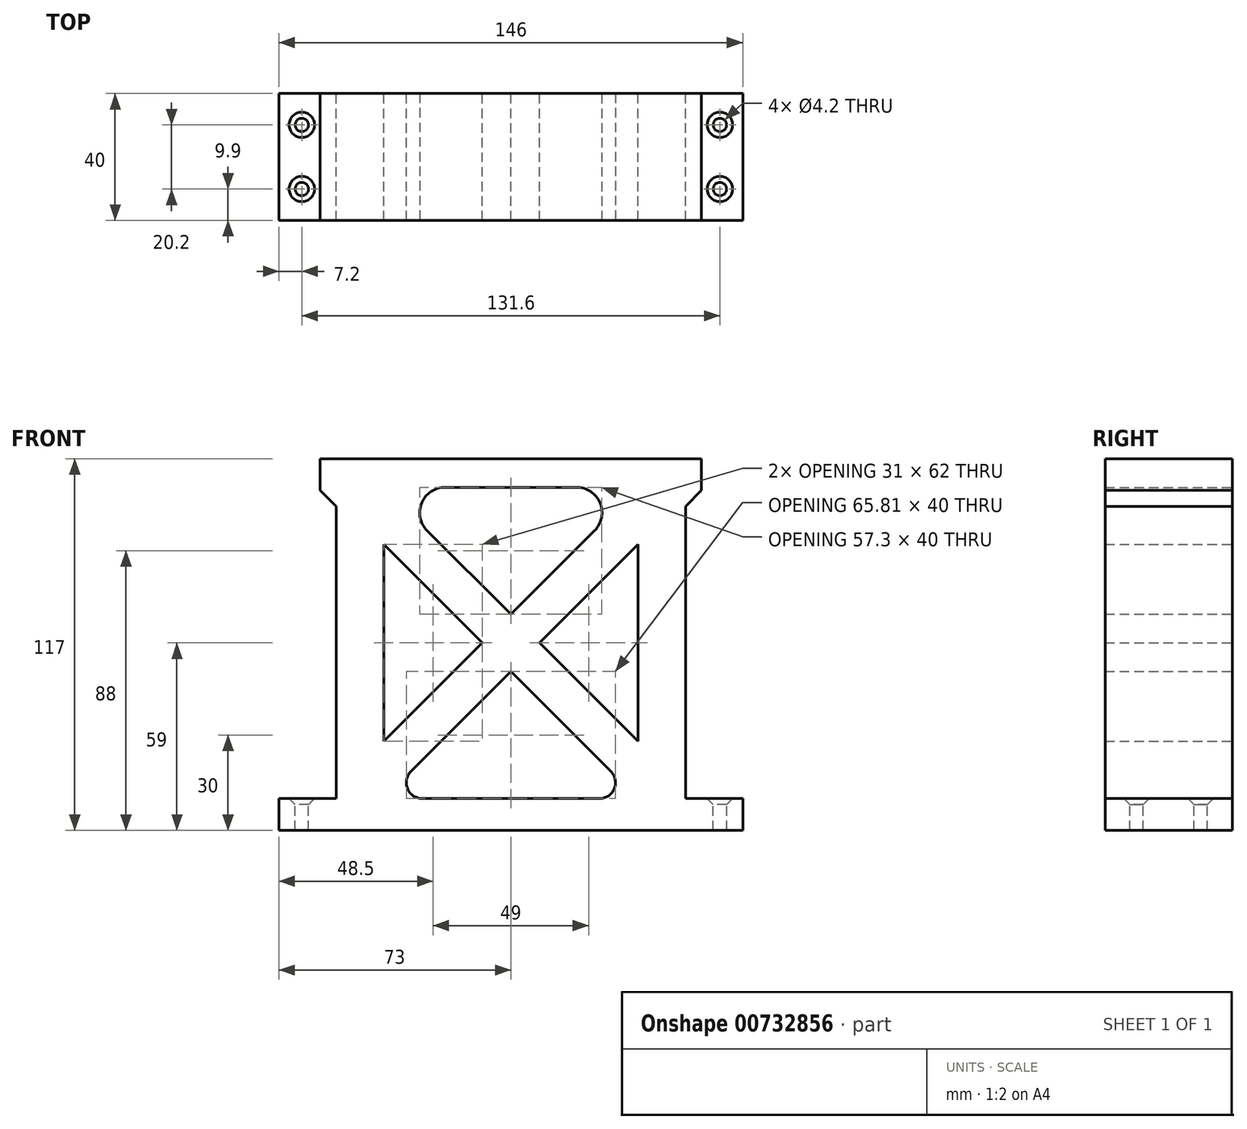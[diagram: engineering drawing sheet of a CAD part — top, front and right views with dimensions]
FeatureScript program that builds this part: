
annotation { "Feature Type Name" : "Feature", "Feature Type Description" : "" }
export const myFeature = defineFeature(function(context is Context, id is Id, definition is map)
    precondition{}
    {
        {
            var Q0;
            Q0=qCreatedBy(makeId("Front.planeOp"),FACE);
            var sketch = newSketch(context, id + "F0", { "sketchPlane" : qUnion([Q0])});
            skLineSegment(sketch, "E0", {"start": v(-73, 0) * mm, "end": v(-73, 10) * mm});
            skLineSegment(sketch, "E1", {"start": v(-73, 10) * mm, "end": v(-55, 10) * mm});
            skLineSegment(sketch, "E2", {"start": v(-55, 10) * mm, "end": v(-55, 107) * mm});
            skLineSegment(sketch, "E3", {"start": v(-55, 107) * mm, "end": v(-60, 107) * mm});
            skLineSegment(sketch, "E4", {"start": v(-60, 107) * mm, "end": v(-60, 117) * mm});
            skLineSegment(sketch, "E5", {"start": v(-60, 117) * mm, "end": v(0, 117) * mm});
            skLineSegment(sketch, "E6", {"start": v(0, 0) * mm, "end": v(-73, 0) * mm});
            skLineSegment(sketch, "E7", {"start": v(-40, 121.48) * mm, "end": v(-40, -14.49) * mm, "construction": true});
            skLineSegment(sketch, "E8", {"start": v(-55, 10) * mm, "end": v(13, 10) * mm, "construction": true});
            skLineSegment(sketch, "E9", {"start": v(-40, 28) * mm, "end": v(15.98, 83.98) * mm, "construction": true});
            skLineSegment(sketch, "E10", {"start": v(-40, 10) * mm, "end": v(0, 50) * mm, "construction": true});
            skLineSegment(sketch, "E11", {"start": v(0, 50) * mm, "end": v(-40, 90) * mm, "construction": true});
            skLineSegment(sketch, "E12", {"start": v(0, 68) * mm, "end": v(-51.64, 119.64) * mm, "construction": true});
            skLineSegment(sketch, "E13", {"start": v(-40, 10) * mm, "end": v(0, 50) * mm});
            skLineSegment(sketch, "E14", {"start": v(-40, 28) * mm, "end": v(-9, 59) * mm});
            skLineSegment(sketch, "E15", {"start": v(-9, 59) * mm, "end": v(-40, 90) * mm});
            skLineSegment(sketch, "E16", {"start": v(-40, 28) * mm, "end": v(-40, 90) * mm});
            skLineSegment(sketch, "E17", {"start": v(0, 68) * mm, "end": v(-40, 108) * mm});
            skLineSegment(sketch, "E18", {"start": v(-40, 108) * mm, "end": v(0, 108) * mm});
            skLineSegment(sketch, "E19", {"start": v(-40, 10) * mm, "end": v(0, 10) * mm});
            skLineSegment(sketch, "E20.MirrorCS", {"start": v(60, 117) * mm, "end": v(0, 117) * mm});
            skLineSegment(sketch, "E21.MirrorCS", {"start": v(60, 107) * mm, "end": v(60, 117) * mm});
            skLineSegment(sketch, "E22.MirrorCS", {"start": v(55, 107) * mm, "end": v(60, 107) * mm});
            skLineSegment(sketch, "E23.MirrorCS", {"start": v(55, 10) * mm, "end": v(55, 107) * mm});
            skLineSegment(sketch, "E24.MirrorCS", {"start": v(40, 28) * mm, "end": v(40, 90) * mm});
            skLineSegment(sketch, "E25.MirrorCS", {"start": v(9, 59) * mm, "end": v(40, 90) * mm});
            skLineSegment(sketch, "E26.MirrorCS", {"start": v(40, 28) * mm, "end": v(9, 59) * mm});
            skLineSegment(sketch, "E27.MirrorCS", {"start": v(40, 10) * mm, "end": v(0, 50) * mm});
            skLineSegment(sketch, "E28.MirrorCS", {"start": v(0, 68) * mm, "end": v(40, 108) * mm});
            skLineSegment(sketch, "E29.MirrorCS", {"start": v(40, 108) * mm, "end": v(0, 108) * mm});
            skLineSegment(sketch, "E30.MirrorCS", {"start": v(40, 10) * mm, "end": v(0, 10) * mm});
            skLineSegment(sketch, "E31.MirrorCS", {"start": v(0, 0) * mm, "end": v(73, 0) * mm});
            skLineSegment(sketch, "E32.MirrorCS", {"start": v(73, 0) * mm, "end": v(73, 10) * mm});
            skLineSegment(sketch, "E33.MirrorCS", {"start": v(73, 10) * mm, "end": v(55, 10) * mm});
            skSolve(sketch);
        }
        {
            var Q0;
            Q0 = qSketchRegion(id + "F0", true);
            extrude(context, id + "F1", {"entities" : qUnion([Q0]), "depth" : 40 * mm, "offsetDistance" : 25 * mm});
        }
        {
            var Q0;
            Q0=makeQuery(id+"F1.opExtrude","SWEPT_EDGE",EDGE,{"disambiguationData":[OSD([sQuery(id+"F0.wireOp",EDGE,"E17"),sQuery(id+"F0.wireOp",EDGE,"E18")])]});
            var Q1;
            Q1=makeQuery(id+"F1.opExtrude","SWEPT_EDGE",EDGE,{"disambiguationData":[OSD([sQuery(id+"F0.wireOp",EDGE,"E28.MirrorCS"),sQuery(id+"F0.wireOp",EDGE,"E29.MirrorCS")])]});
            fillet(context, id + "F2", {"entities" : qUnion([Q0, Q1]), "radius" : 8 * mm, "tangentPropagation" : true, "allowEdgeOverflow" : false});
        }
        {
            var Q0;
            Q0=makeQuery(id+"F1.opExtrude","SWEPT_EDGE",EDGE,{"disambiguationData":[OSD([sQuery(id+"F0.wireOp",EDGE,"E13"),sQuery(id+"F0.wireOp",EDGE,"E19")])]});
            var Q1;
            Q1=makeQuery(id+"F1.opExtrude","SWEPT_EDGE",EDGE,{"disambiguationData":[OSD([sQuery(id+"F0.wireOp",EDGE,"E27.MirrorCS"),sQuery(id+"F0.wireOp",EDGE,"E30.MirrorCS")])]});
            fillet(context, id + "F3", {"entities" : qUnion([Q0, Q1]), "radius" : 5 * mm, "tangentPropagation" : true, "allowEdgeOverflow" : false});
        }
        {
            var Q0;
            Q0=makeQuery(id+"F1.opExtrude","SWEPT_FACE",FACE,{"disambiguationData":[OSD([sQuery(id+"F0.wireOp",EDGE,"E1")])]});
            var sketch = newSketch(context, id + "F4", { "sketchPlane" : qUnion([Q0])});
            skPoint(sketch, "E34", {"position": v(-65.8, -9.9) * mm});
            skPoint(sketch, "E35", {"position": v(-65.8, -30.1) * mm});
            skPoint(sketch, "E36", {"position": v(65.8, -30.1) * mm});
            skPoint(sketch, "E37", {"position": v(65.8, -9.9) * mm});
            skLineSegment(sketch, "E38", {"start": v(-85.7, -20) * mm, "end": v(95.67, -20) * mm, "construction": true});
            skPoint(sketch, "E38.startSnap0", {"position": v(-73, -20) * mm});
            skSolve(sketch);
        }
        {
            var Q0;
            Q0=sQuery(id+"F4.wireOp",VERTEX,"E34");
            var Q1;
            Q1=sQuery(id+"F4.wireOp",VERTEX,"E35");
            var Q2;
            Q2=sQuery(id+"F4.wireOp",VERTEX,"E36");
            var Q3;
            Q3=sQuery(id+"F4.wireOp",VERTEX,"E37");
            var Q4;
            Q4=makeQuery(id+"F1.opExtrude","SWEPT_BODY",BODY,{"disambiguationData":[OSD([sQuery(id+"F0.wireOp",EDGE,"E0"),sQuery(id+"F0.wireOp",EDGE,"E1"),sQuery(id+"F0.wireOp",EDGE,"E2"),sQuery(id+"F0.wireOp",EDGE,"E3"),sQuery(id+"F0.wireOp",EDGE,"E4"),sQuery(id+"F0.wireOp",EDGE,"E5"),sQuery(id+"F0.wireOp",EDGE,"E6"),sQuery(id+"F0.wireOp",EDGE,"E13"),sQuery(id+"F0.wireOp",EDGE,"E14"),sQuery(id+"F0.wireOp",EDGE,"E15"),sQuery(id+"F0.wireOp",EDGE,"E16"),sQuery(id+"F0.wireOp",EDGE,"E17"),sQuery(id+"F0.wireOp",EDGE,"E18"),sQuery(id+"F0.wireOp",EDGE,"E19"),sQuery(id+"F0.wireOp",EDGE,"E20.MirrorCS"),sQuery(id+"F0.wireOp",EDGE,"E21.MirrorCS"),sQuery(id+"F0.wireOp",EDGE,"E22.MirrorCS"),sQuery(id+"F0.wireOp",EDGE,"E23.MirrorCS"),sQuery(id+"F0.wireOp",EDGE,"E24.MirrorCS"),sQuery(id+"F0.wireOp",EDGE,"E25.MirrorCS"),sQuery(id+"F0.wireOp",EDGE,"E26.MirrorCS"),sQuery(id+"F0.wireOp",EDGE,"E27.MirrorCS"),sQuery(id+"F0.wireOp",EDGE,"E28.MirrorCS"),sQuery(id+"F0.wireOp",EDGE,"E29.MirrorCS"),sQuery(id+"F0.wireOp",EDGE,"E30.MirrorCS"),sQuery(id+"F0.wireOp",EDGE,"E31.MirrorCS"),sQuery(id+"F0.wireOp",EDGE,"E32.MirrorCS"),sQuery(id+"F0.wireOp",EDGE,"E33.MirrorCS")])]});
            hole(context, id + "F5", {"style" : HoleStyle.C_SINK, "endStyle" : HoleEndStyle.THROUGH, "holeDiameter" : 4.2 * mm, "cSinkDiameter" : 8 * mm, "cSinkAngle" : 90 * degree, "majorDiameter" : 5 * mm, "isTappedThrough" : true, "tappedDepth" : 12 * mm, "tapClearance" : 3, "startFromSketch" : true, "locations" : qUnion([Q0, Q1, Q2, Q3]), "scope" : qUnion([Q4])});
        }
        {
            var Q0;
            Q0=makeQuery(id+"F1.opExtrude","SWEPT_EDGE",EDGE,{"disambiguationData":[OSD([sQuery(id+"F0.wireOp",EDGE,"E2"),sQuery(id+"F0.wireOp",EDGE,"E3")])]});
            var Q1;
            Q1=makeQuery(id+"F1.opExtrude","SWEPT_EDGE",EDGE,{"disambiguationData":[OSD([sQuery(id+"F0.wireOp",EDGE,"E22.MirrorCS"),sQuery(id+"F0.wireOp",EDGE,"E23.MirrorCS")])]});
            chamfer(context, id + "F6", {"entities" : qUnion([Q0, Q1]), "width" : 5 * mm, "tangentPropagation" : true});
        }
    });
